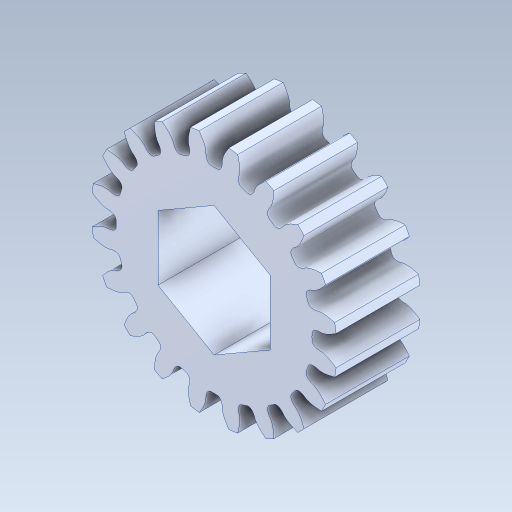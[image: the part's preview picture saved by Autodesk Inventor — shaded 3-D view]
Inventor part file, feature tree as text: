
AUTODESK INVENTOR PART (.ipt)
format: ipt  version: 2024 (Build 280153000, 153)  size: 692,224 bytes
history: native  units: in
note: dims shown in document units (in); Inventor stores cm internally (conversion verified against a paired STEP export)
features: extrude x2, sketch x2, other x1
ambient origin geometry x8: Origin, YZ Plane, XZ Plane, XY Plane, X Axis, Y Axis, Z Axis, Center Point
bodies: Solid1 (feature_tree)
feature tree (5):
  extrude  "Extrusion1"  Depth=1.0in TaperAngle=0.0deg
  extrude  "Extrusion2"  [1 undecoded]
  sketch  "Sketch1"  dims[d0=1.0in d1=0.0in d2=1.0in d3=0.0in]
  sketch  "Sketch2"
  other  "Boss-Extrude1"
note: 1 required parameter value undecoded (feature->parameter linkage not recoverable at this tier; creation-order binding heuristic only, values carry confidence <= 0.55)
